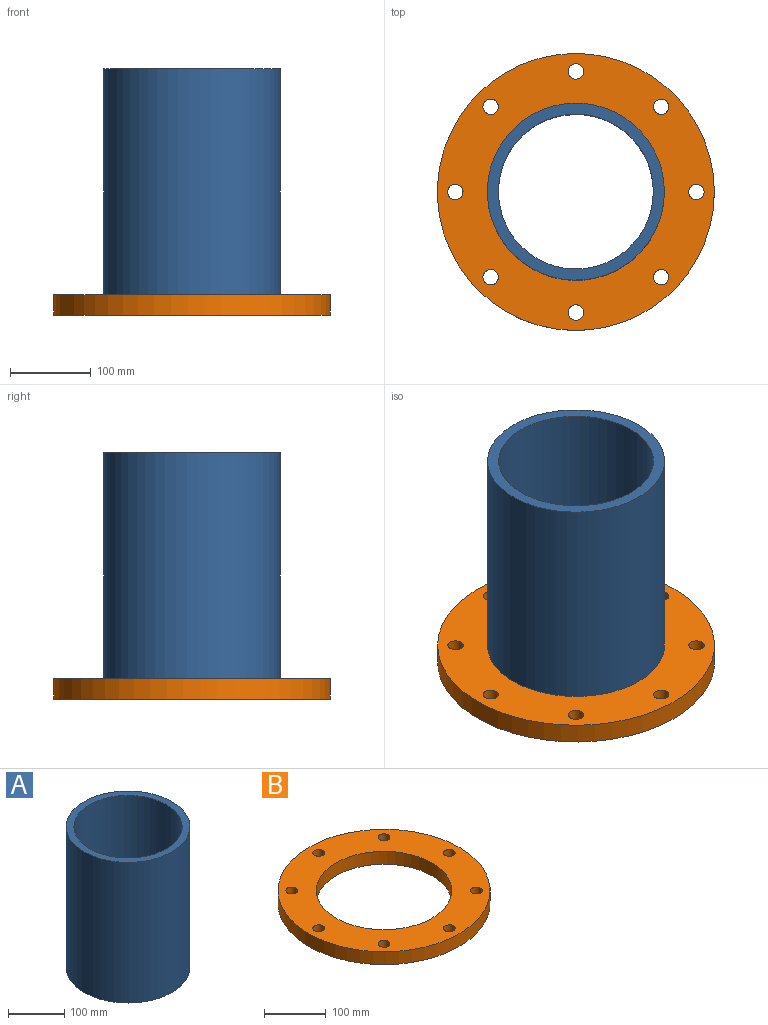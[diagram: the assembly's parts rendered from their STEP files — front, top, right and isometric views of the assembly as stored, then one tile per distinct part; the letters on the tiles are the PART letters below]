
ASSEMBLY  parts=2 mates=1
PART A: 4 faces, bbox 219.2x219.2x304.8 mm
  f0: cylinder r=95.87mm len=304.8mm, axis (0,0,-1), area 183606.5mm2, adj f2,f3
  f1: cylinder r=109.6mm len=304.8mm, axis (0,0,-1), area 209898.5mm2, adj f2,f3
  f2: plane 219.2x219.2mm, normal (0,0,1), area 8862.1mm2, adj f0,f1
  f3: plane 219.2x219.2mm, normal (0,0,-1), area 8862.1mm2, adj f0,f1
PART B: 12 faces, bbox 342.9x342.9x25.4 mm
  f0: cylinder r=109.6mm len=219.2mm, axis (0,0,-1), area 17491.5mm2, adj f2,f3
  f1: cylinder r=171.45mm len=342.9mm, axis (0,0,-1), area 27362.2mm2, adj f2,f3
  f2: plane 342.9x342.9mm, normal (0,0,1), area 52329.3mm2, adj f0,f1,f4,f5,f6,f7,f8,f9
  f3: plane 342.9x342.9mm, normal (0,0,-1), area 52329.3mm2, adj f0,f1,f4,f5,f6,f7,f8,f9
  f4: cylinder r=9.53mm len=25.4mm, axis (0,0,1), area 1520.1mm2, adj f2,f3
  f5: cylinder r=9.53mm len=25.4mm, axis (0,0,1), area 1520.1mm2, adj f2,f3
  f6: cylinder r=9.53mm len=25.4mm, axis (0,0,1), area 1520.1mm2, adj f2,f3
  f7: cylinder r=9.53mm len=25.4mm, axis (0,0,1), area 1520.1mm2, adj f2,f3
  f8: cylinder r=9.53mm len=25.4mm, axis (0,0,1), area 1520.1mm2, adj f2,f3
  f9: cylinder r=9.53mm len=25.4mm, axis (0,0,1), area 1520.1mm2, adj f2,f3
  f10: cylinder r=9.53mm len=25.4mm, axis (0,0,1), area 1520.1mm2, adj f2,f3
  f11: cylinder r=9.53mm len=25.4mm, axis (0,0,1), area 1520.1mm2, adj f2,f3
PLACE A at identity
PLACE B at identity
MATE fastened B.f0 <-> A.f0  axis (0,0,-1) through (0,0,0)mm
